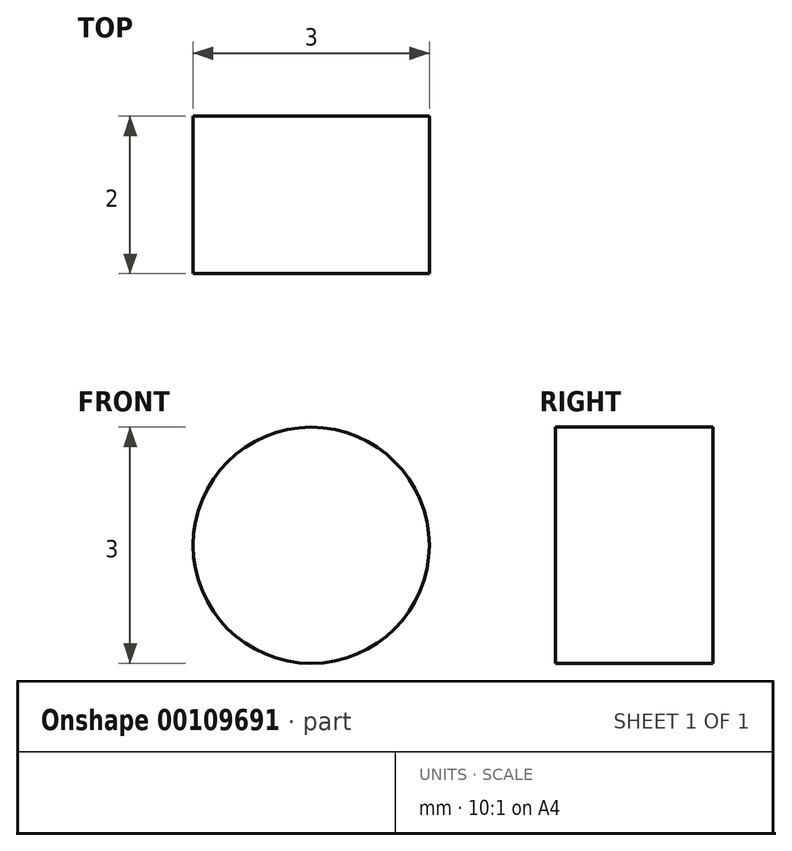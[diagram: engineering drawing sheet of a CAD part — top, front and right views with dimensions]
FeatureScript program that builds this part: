
annotation { "Feature Type Name" : "Feature", "Feature Type Description" : "" }
export const myFeature = defineFeature(function(context is Context, id is Id, definition is map)
    precondition{}
    {
        {
            var Q0;
            Q0=qCreatedBy(makeId("Front.planeOp"),FACE);
            var sketch = newSketch(context, id + "F0", { "sketchPlane" : qUnion([Q0])});
            skCircle(sketch, "E0", {"center": v(0, 0) * mm, "radius": 1.5 * mm});
            skSolve(sketch);
        }
        {
            var Q0;
            Q0 = qSketchRegion(id + "F0", true);
            extrude(context, id + "F1", {"entities" : qUnion([Q0]), "depth" : 2 * mm});
        }
    });
